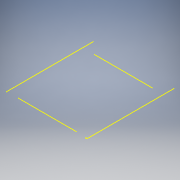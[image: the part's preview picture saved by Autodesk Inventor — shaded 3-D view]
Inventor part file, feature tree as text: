
AUTODESK INVENTOR PART (.ipt)
format: ipt  version: 2016 (Build 200138000, 138)  size: 299,520 bytes
history: native  units: mm
features: reference x8, other x4, sketch x3, sheet_metal_op x1
ambient origin geometry x8: Origin, YZ Plane, XZ Plane, XY Plane, X Axis, Y Axis, Z Axis, Center Point
bodies: Solid1 (feature_tree)
feature tree (16):
  sheet_metal_op  "Face1"
  other  "Corner Chamfer1"
  sketch  "Sketch1"  dims[d0=3.0mm]
  reference  "Reference1"
  reference  "Reference5"
  reference  "Reference6"
  reference  "Reference7"
  other  "Plate1"
  sketch  "Sketch3"  dims[d1=3.0mm]
  reference  "Reference12"
  reference  "Reference13"
  reference  "Reference14"
  reference  "Reference15"
  sketch  "Sketch4"  dims[d2=3.0mm d4=1.0mm d5=2.0mm d6=6.0mm d7=45.0deg d8=1.0mm d9=1.0mm d10=1.0mm d11=1.0mm d33=3.0mm d34=4.0mm d35=2.2mm d36=4.0mm d37=2.2mm d38=4.0mm d39=2.2mm d40=4.0mm d41=2.2mm d42=1.0mm d43=0.0mm d44=76.0mm d45=2.0mm d46=50.0mm d47=120.0mm d48=20.0mm d50=100.0mm d51=140.0mm d53=8.0mm d56=1.0mm d57=0.0mm]
  other  "Cut2"
  other  "Cut3"
